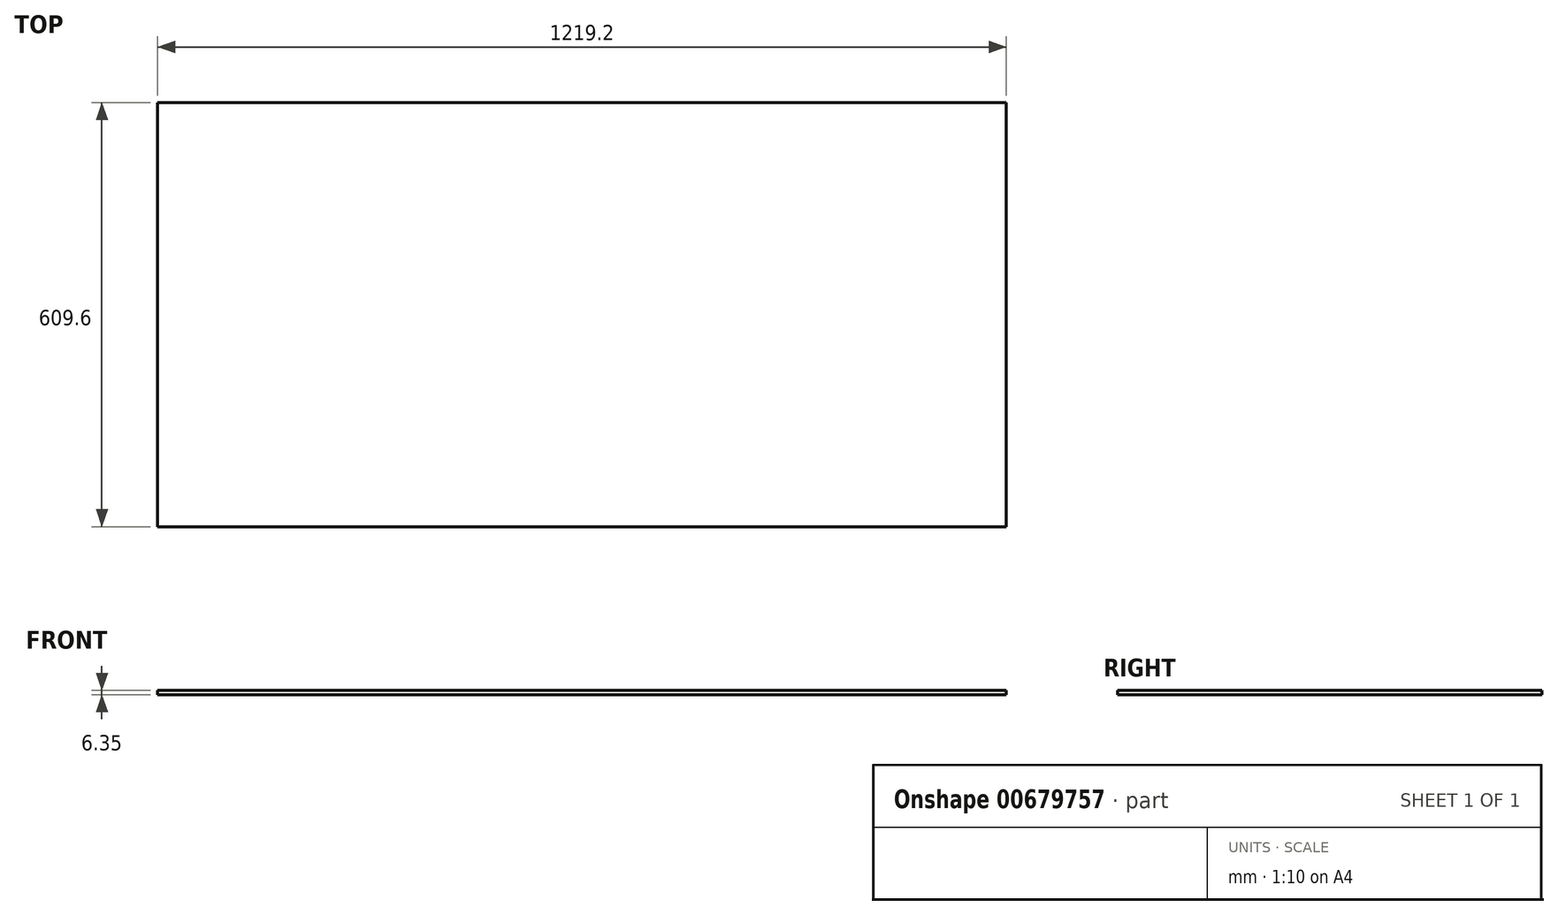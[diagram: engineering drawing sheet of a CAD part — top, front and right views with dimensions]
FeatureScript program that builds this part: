
annotation { "Feature Type Name" : "Feature", "Feature Type Description" : "" }
export const myFeature = defineFeature(function(context is Context, id is Id, definition is map)
    precondition{}
    {
        {
            var Q0;
            Q0=qCreatedBy(makeId("Top.planeOp"),FACE);
            var sketch = newSketch(context, id + "F0", { "sketchPlane" : qUnion([Q0])});
            skLineSegment(sketch, "E0.bottom", {"start": v(609.6, 304.8) * mm, "end": v(-609.6, 304.8) * mm});
            skLineSegment(sketch, "E0.top", {"start": v(609.6, -304.8) * mm, "end": v(-609.6, -304.8) * mm});
            skLineSegment(sketch, "E0.left", {"start": v(609.6, 304.8) * mm, "end": v(609.6, -304.8) * mm});
            skLineSegment(sketch, "E0.right", {"start": v(-609.6, 304.8) * mm, "end": v(-609.6, -304.8) * mm});
            skPoint(sketch, "E0.middle", {"position": v(0, 0) * mm});
            skSolve(sketch);
        }
        {
            var Q0;
            Q0=makeQuery(id+"F0.imprint","IMPRINT",FACE,{"disambiguationData":[TD([[makeQuery(id+"F0.imprint","IMPRINT",EDGE,{"derivedFrom":sQuery(id+"F0.wireOp",EDGE,"E0.bottom")}),1.0]])]});
            extrude(context, id + "F1", {"entities" : qUnion([Q0]), "depth" : 6.35 * mm, "offsetDistance" : 25.4 * mm});
        }
    });
